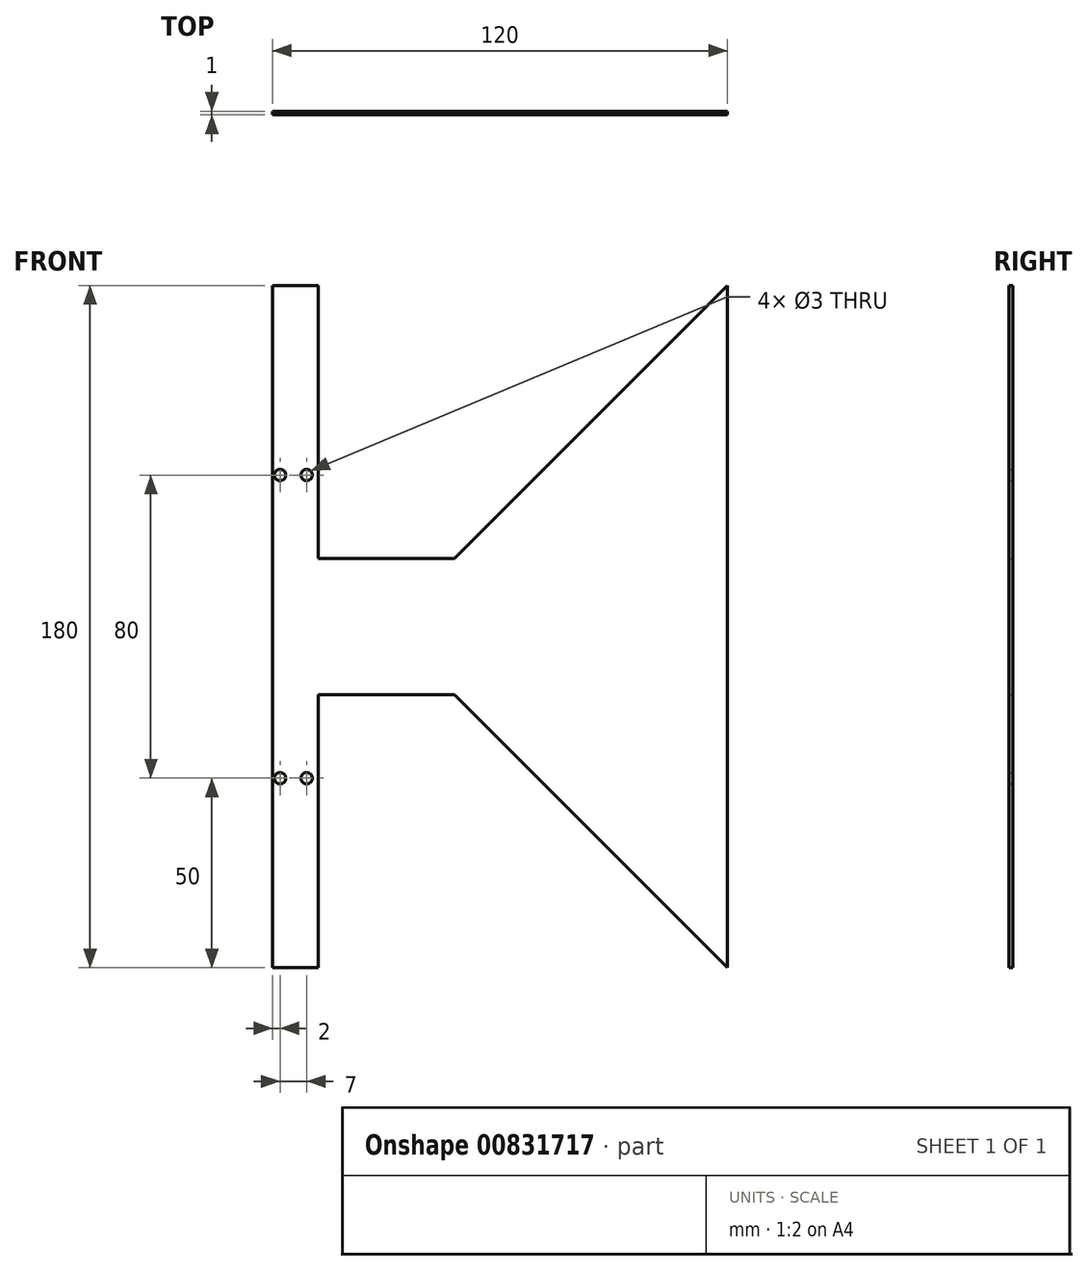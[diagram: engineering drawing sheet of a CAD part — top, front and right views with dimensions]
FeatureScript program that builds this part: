
annotation { "Feature Type Name" : "Feature", "Feature Type Description" : "" }
export const myFeature = defineFeature(function(context is Context, id is Id, definition is map)
    precondition{}
    {
        {
            var Q0;
            Q0=qCreatedBy(makeId("Front.planeOp"),FACE);
            var sketch = newSketch(context, id + "F0", { "sketchPlane" : qUnion([Q0])});
            skLineSegment(sketch, "E0.bottom", {"start": v(0, 90) * mm, "end": v(12, 90) * mm});
            skLineSegment(sketch, "E0.top", {"start": v(0, -90) * mm, "end": v(12, -90) * mm});
            skLineSegment(sketch, "E0.left", {"start": v(0, 90) * mm, "end": v(0, -90) * mm});
            skLineSegment(sketch, "E0.right", {"start": v(12, 90) * mm, "end": v(12, -90) * mm});
            skCircle(sketch, "E1", {"center": v(2, 40) * mm, "radius": 1.5 * mm});
            skCircle(sketch, "E2", {"center": v(9, 40) * mm, "radius": 1.5 * mm});
            skCircle(sketch, "E3", {"center": v(2, -40) * mm, "radius": 1.5 * mm});
            skCircle(sketch, "E4", {"center": v(9, -40) * mm, "radius": 1.5 * mm});
            skLineSegment(sketch, "E5.bottom", {"start": v(12, 18) * mm, "end": v(48, 18) * mm});
            skLineSegment(sketch, "E5.top", {"start": v(12, -18) * mm, "end": v(48, -18) * mm});
            skLineSegment(sketch, "E5.left", {"start": v(12, 18) * mm, "end": v(12, -18) * mm});
            skLineSegment(sketch, "E5.right", {"start": v(48, 18) * mm, "end": v(48, -18) * mm});
            skLineSegment(sketch, "E6", {"start": v(48, 18) * mm, "end": v(120, 90) * mm});
            skLineSegment(sketch, "E7", {"start": v(48, -18) * mm, "end": v(120, -90) * mm});
            skLineSegment(sketch, "E8", {"start": v(120, 90) * mm, "end": v(120, -90) * mm});
            skSolve(sketch);
        }
        {
            var Q0;
            {var subQ1=sQuery(id+"F0.wireOp",EDGE,"E0.bottom");Q0=makeQuery(id+"F0.imprint","IMPRINT",FACE,{"disambiguationData":[TD([[makeQuery(id+"F0.imprint","IMPRINT",EDGE,{"derivedFrom":subQ1}),-1.0]])]});}
            var Q1;
            Q1=makeQuery(id+"F0.imprint","IMPRINT",FACE,{"disambiguationData":[TD([[makeQuery(id+"F0.imprint","IMPRINT",EDGE,{"derivedFrom":sQuery(id+"F0.wireOp",EDGE,"E5.bottom")}),-1.0]])]});
            var Q2;
            Q2=makeQuery(id+"F0.imprint","IMPRINT",FACE,{"disambiguationData":[TD([[makeQuery(id+"F0.imprint","IMPRINT",EDGE,{"derivedFrom":sQuery(id+"F0.wireOp",EDGE,"E5.right")}),1.0]])]});
            extrude(context, id + "F1", {"entities" : qUnion([Q0, Q1, Q2]), "endBound" : BoundingType.SYMMETRIC, "depth" : 1 * mm, "offsetDistance" : 25 * mm});
        }
    });
